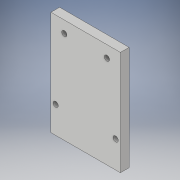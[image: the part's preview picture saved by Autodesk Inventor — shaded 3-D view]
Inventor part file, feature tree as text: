
AUTODESK INVENTOR PART (.ipt)
format: ipt  version: 2018 (Build 220112000, 112)  size: 116,224 bytes
history: native  units: in
note: dims shown in document units (in); Inventor stores cm internally (conversion verified against a paired STEP export)
features: extrude x2, sketch x2
ambient origin geometry x8: Origin, YZ Plane, XZ Plane, XY Plane, X Axis, Y Axis, Z Axis, Center Point
bodies: Solid1 (feature_tree)
feature tree (4):
  extrude  "Extrusion1"  Depth=2.3622in
  extrude  "Extrusion2"  Depth=0.1969in
  sketch  "Sketch1"  dims[d0=1.5748in d1=2.3622in]
  sketch  "Sketch2"  dims[d2=0.1969in d3=0.0in d4=0.6102in d5=0.1181in d6=0.1181in d9=0.2657in d12=0.1181in d13=0.1181in d14=1.0in d15=0.0in d16=1.3583in d17=0.6791in d18=0.6791in d19=0.9646in d20=0.4823in d21=0.4823in]
